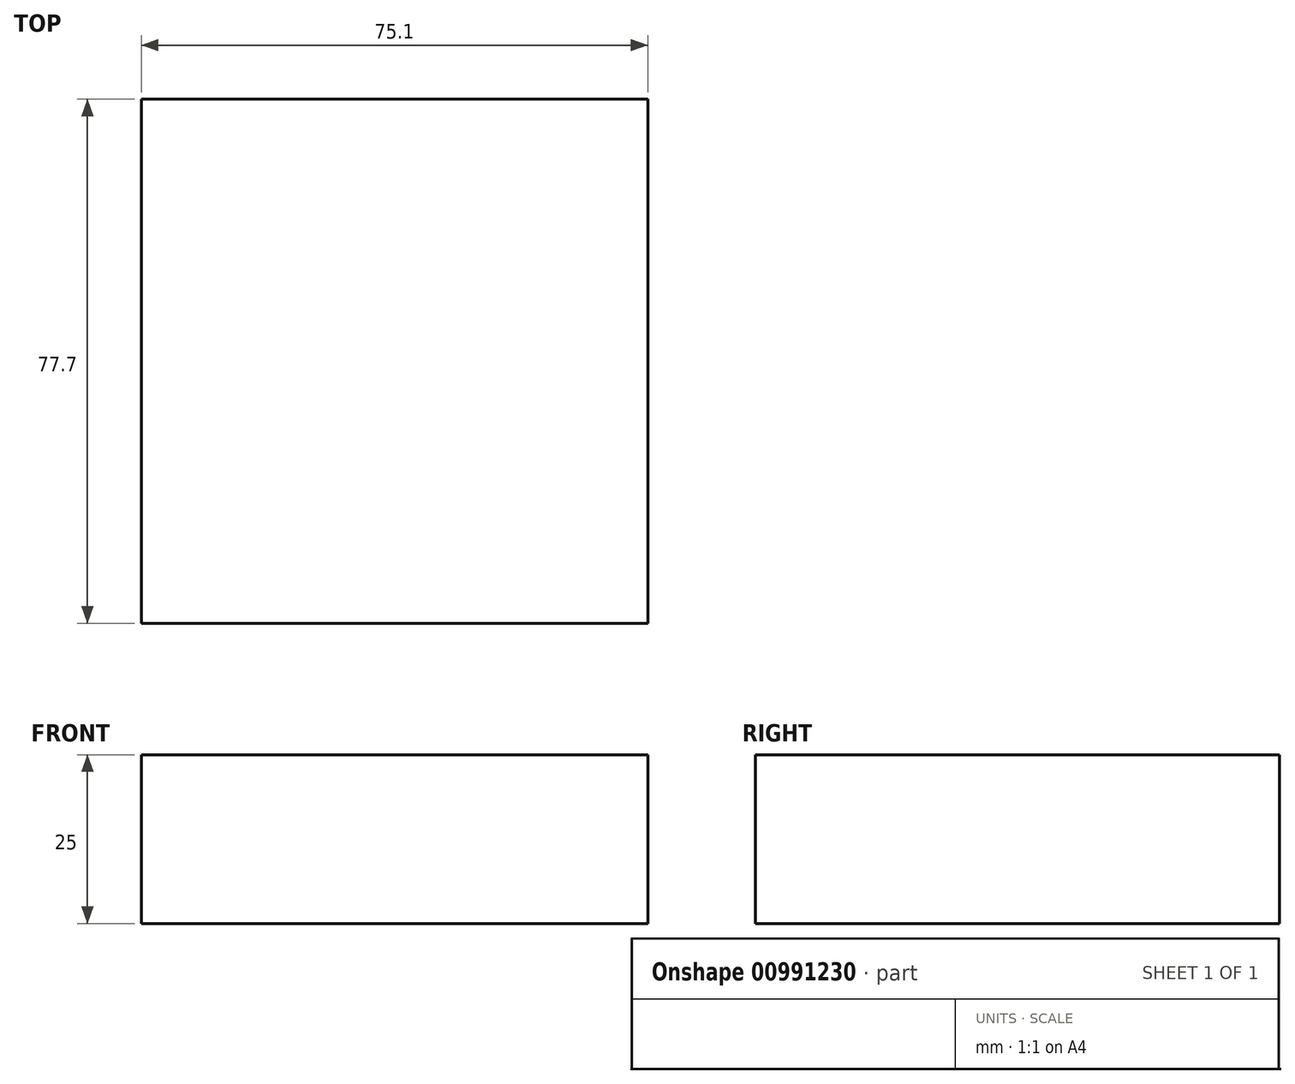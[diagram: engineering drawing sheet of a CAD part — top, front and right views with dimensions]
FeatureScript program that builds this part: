
annotation { "Feature Type Name" : "Feature", "Feature Type Description" : "" }
export const myFeature = defineFeature(function(context is Context, id is Id, definition is map)
    precondition{}
    {
        {
            var Q0;
            Q0=qCreatedBy(makeId("Top.planeOp"),FACE);
            var sketch = newSketch(context, id + "F0", { "sketchPlane" : qUnion([Q0])});
            skLineSegment(sketch, "E0.bottom", {"start": v(37.55, -38.85) * mm, "end": v(-37.55, -38.85) * mm});
            skLineSegment(sketch, "E0.top", {"start": v(37.55, 38.85) * mm, "end": v(-37.55, 38.85) * mm});
            skLineSegment(sketch, "E0.left", {"start": v(37.55, -38.85) * mm, "end": v(37.55, 38.85) * mm});
            skLineSegment(sketch, "E0.right", {"start": v(-37.55, -38.85) * mm, "end": v(-37.55, 38.85) * mm});
            skPoint(sketch, "E0.middle", {"position": v(0, 0) * mm});
            skSolve(sketch);
        }
        {
            var Q0;
            Q0=makeQuery(id+"F0.imprint","IMPRINT",FACE,{"disambiguationData":[TD([[makeQuery(id+"F0.imprint","IMPRINT",EDGE,{"derivedFrom":sQuery(id+"F0.wireOp",EDGE,"E0.bottom")}),-1.0]])]});
            extrude(context, id + "F1", {"entities" : qUnion([Q0]), "depth" : 25 * mm, "offsetDistance" : 25 * mm});
        }
    });
